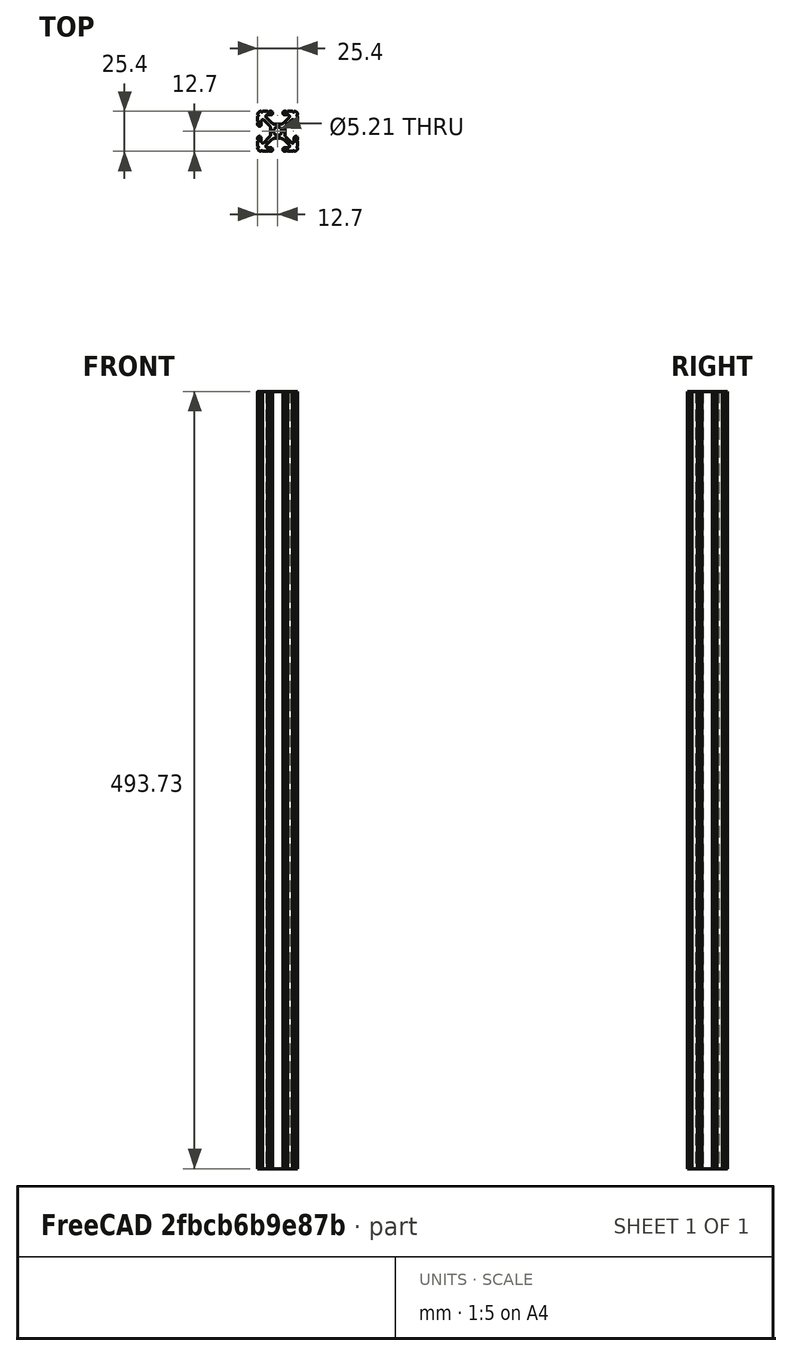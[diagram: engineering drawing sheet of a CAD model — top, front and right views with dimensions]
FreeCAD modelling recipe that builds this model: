
FCSTD DOCUMENT  (FreeCAD 0.18R4 (GitTag))
Label: 1010-19p438
License: All rights reserved
LicenseURL: http://en.wikipedia.org/wiki/All_rights_reserved
objects: Sketcher::SketchObject×1, Part::Extrusion×1
note: 2 computed .brp shape members not serialized (recipe doc carries the construction recipe); baked Part::Feature solids carry a one-line shape summary decoded from their .brp

FEATURE [Sketcher::SketchObject] Sketch097
  sketch-geometry (97):
    g0: Circle CenterX=0 CenterY=0 CenterZ=0 NormalX=0 NormalY=0 NormalZ=-1 AngleXU=0 Radius=2.6035
    g1: ArcOfCircle CenterX=12.7 CenterY=5.82508 CenterZ=0 NormalX=0 NormalY=0 NormalZ=1 AngleXU=0 Radius=0.508 StartAngle=1.5708 EndAngle=4.71239
    g2: LineSegment StartX=3.2385 StartY=11.651 StartZ=0 EndX=3.2385 EndY=11.5392 EndZ=0
    g3: LineSegment StartX=6.33313 StartY=-12.7 StartZ=0 EndX=9.55044 EndY=-12.7 EndZ=0
    g4: LineSegment StartX=7.20704 StartY=8.72437 StartZ=0 EndX=3.89827 EndY=5.42317 EndZ=0
    g5: ArcOfCircle CenterX=7.6835 CenterY=1.59319 CenterZ=0 NormalX=0 NormalY=0 NormalZ=1 AngleXU=0 Radius=3.175 StartAngle=2.35505 EndAngle=3.14159
    g6: ArcOfCircle CenterX=-1.70925 CenterY=-7.6708 CenterZ=0 NormalX=0 NormalY=0 NormalZ=1 AngleXU=0 Radius=3.175 StartAngle=1.5708 EndAngle=2.35528
    g7: ArcOfCircle CenterX=11.5392 CenterY=-4.28747 CenterZ=0 NormalX=0 NormalY=0 NormalZ=1 AngleXU=0 Radius=1.04901 StartAngle=1.5708 EndAngle=3.14159
    g8: ArcOfCircle CenterX=12.7 CenterY=-5.82508 CenterZ=0 NormalX=0 NormalY=0 NormalZ=1 AngleXU=0 Radius=0.508 StartAngle=1.5708 EndAngle=4.71239
    g9: LineSegment StartX=4.28751 StartY=10.4902 StartZ=0 EndX=6.47679 EndY=10.4902 EndZ=0
    g10: ArcOfCircle CenterX=4.28751 CenterY=11.651 CenterZ=0 NormalX=0 NormalY=0 NormalZ=1 AngleXU=0 Radius=1.04901 StartAngle=1.5708 EndAngle=3.14159
    g11: ArcOfCircle CenterX=6.47679 CenterY=9.45629 CenterZ=0 NormalX=0 NormalY=0 NormalZ=1 AngleXU=0 Radius=1.03391 StartAngle=5.49664 EndAngle=7.85398
    g12: ArcOfCircle CenterX=4.28751 CenterY=11.5392 CenterZ=0 NormalX=0 NormalY=0 NormalZ=1 AngleXU=0 Radius=1.04901 StartAngle=3.14159 EndAngle=4.71239
    g13: LineSegment StartX=3.95227 StartY=-5.42369 StartZ=0 EndX=7.17965 EndY=-8.64519 EndZ=0
    g14: ArcOfCircle CenterX=11.651 CenterY=4.28747 CenterZ=0 NormalX=0 NormalY=0 NormalZ=1 AngleXU=0 Radius=1.04901 StartAngle=4.71239 EndAngle=6.28319
    g15: ArcOfCircle CenterX=-5.82513 CenterY=-12.7 CenterZ=0 NormalX=0 NormalY=0 NormalZ=1 AngleXU=0 Radius=0.508 StartAngle=0 EndAngle=3.14159
    g16: LineSegment StartX=-6.47679 StartY=10.4902 StartZ=0 EndX=-4.28751 EndY=10.4902 EndZ=0
    g17: ArcOfCircle CenterX=-12.7 CenterY=10.0584 CenterZ=0 NormalX=0 NormalY=0 NormalZ=1 AngleXU=0 Radius=0.508 StartAngle=4.71239 EndAngle=7.85368
    g18: ArcOfCircle CenterX=-12.7 CenterY=5.82508 CenterZ=0 NormalX=0 NormalY=0 NormalZ=1 AngleXU=0 Radius=0.508 StartAngle=4.71239 EndAngle=7.85398
    g19: LineSegment StartX=-11.5392 StartY=-3.23846 StartZ=0 EndX=-11.651 EndY=-3.23846 EndZ=0
    g20: LineSegment StartX=-3.89827 StartY=5.42317 StartZ=0 EndX=-7.20704 EndY=8.72437 EndZ=0
    g21: LineSegment StartX=1.65578 StartY=4.4958 StartZ=0 EndX=-1.65578 EndY=4.4958 EndZ=0
    g22: ArcOfCircle CenterX=-1.65578 CenterY=7.6708 CenterZ=0 NormalX=0 NormalY=0 NormalZ=1 AngleXU=0 Radius=3.175 StartAngle=3.92813 EndAngle=4.71239
    g23: LineSegment StartX=-9.55044 StartY=-12.7 StartZ=0 EndX=-6.33313 EndY=-12.7 EndZ=0
    g24: ArcOfCircle CenterX=-5.82513 CenterY=12.7 CenterZ=0 NormalX=0 NormalY=0 NormalZ=1 AngleXU=0 Radius=0.508 StartAngle=3.14159 EndAngle=6.28319
    g25: ArcOfCircle CenterX=-4.28751 CenterY=11.651 CenterZ=0 NormalX=0 NormalY=0 NormalZ=1 AngleXU=0 Radius=1.04901 StartAngle=0 EndAngle=1.5708
    g26: LineSegment StartX=-12.7 StartY=-4.28747 StartZ=0 EndX=-12.7 EndY=-5.31708 EndZ=0
    g27: ArcOfCircle CenterX=-6.47679 CenterY=9.45629 CenterZ=0 NormalX=0 NormalY=0 NormalZ=1 AngleXU=0 Radius=1.03391 StartAngle=1.5708 EndAngle=3.92813
    g28: ArcOfCircle CenterX=-4.28751 CenterY=11.5392 CenterZ=0 NormalX=0 NormalY=0 NormalZ=1 AngleXU=0 Radius=1.04901 StartAngle=4.71239 EndAngle=6.28319
    g29: LineSegment StartX=-5.44101 StartY=-3.84082 StartZ=0 EndX=-8.73713 EndY=-7.12941 EndZ=0
    g30: ArcOfCircle CenterX=-7.6835 CenterY=-1.59319 CenterZ=0 NormalX=0 NormalY=0 NormalZ=1 AngleXU=0 Radius=3.175 StartAngle=5.49664 EndAngle=6.28319
    g31: LineSegment StartX=-12.7 StartY=5.31708 StartZ=0 EndX=-12.7 EndY=4.28747 EndZ=0
    g32: LineSegment StartX=-8.73713 StartY=7.12941 StartZ=0 EndX=-5.44101 EndY=3.84082 EndZ=0
    g33: LineSegment StartX=-11.651 StartY=3.23846 StartZ=0 EndX=-11.5392 EndY=3.23846 EndZ=0
    g34: ArcOfCircle CenterX=-9.46279 CenterY=-6.40209 CenterZ=0 NormalX=0 NormalY=0 NormalZ=1 AngleXU=0 Radius=1.02741 StartAngle=3.14159 EndAngle=5.49664
    g35: ArcOfCircle CenterX=-10.5918 CenterY=10.5918 CenterZ=0 NormalX=0 NormalY=0 NormalZ=1 AngleXU=0 Radius=2.1082 StartAngle=1.55877 EndAngle=3.15364
    g36: LineSegment StartX=-12.7 StartY=9.5504 StartZ=0 EndX=-12.7 EndY=6.33308 EndZ=0
    g37: LineSegment StartX=-6.33313 StartY=12.7 StartZ=0 EndX=-9.55044 EndY=12.7 EndZ=0
    g38: ArcOfCircle CenterX=-11.5392 CenterY=-4.28747 CenterZ=0 NormalX=0 NormalY=0 NormalZ=1 AngleXU=0 Radius=1.04901 StartAngle=0 EndAngle=1.5708
    g39: LineSegment StartX=4.28751 StartY=-12.7 StartZ=0 EndX=5.31713 EndY=-12.7 EndZ=0
    g40: LineSegment StartX=5.44101 StartY=3.84082 StartZ=0 EndX=8.73713 EndY=7.12941 EndZ=0
    g41: LineSegment StartX=10.4902 StartY=-4.28747 StartZ=0 EndX=10.4902 EndY=-6.40209 EndZ=0
    g42: ArcOfCircle CenterX=9.46279 CenterY=6.40209 CenterZ=0 NormalX=0 NormalY=0 NormalZ=1 AngleXU=0 Radius=1.02741 StartAngle=0 EndAngle=2.35505
    g43: ArcOfCircle CenterX=5.82513 CenterY=-12.7 CenterZ=0 NormalX=0 NormalY=0 NormalZ=1 AngleXU=0 Radius=0.508 StartAngle=0 EndAngle=3.14159
    g44: LineSegment StartX=12.7 StartY=-9.5504 StartZ=0 EndX=12.7 EndY=-6.33308 EndZ=0
    g45: LineSegment StartX=4.5085 StartY=-1.59319 StartZ=0 EndX=4.5085 EndY=1.59319 EndZ=0
    g46: ArcOfCircle CenterX=12.7 CenterY=10.0584 CenterZ=0 NormalX=0 NormalY=0 NormalZ=1 AngleXU=0 Radius=0.508 StartAngle=1.5711 EndAngle=4.71239
    g47: ArcOfCircle CenterX=12.7 CenterY=-10.0584 CenterZ=0 NormalX=0 NormalY=0 NormalZ=1 AngleXU=0 Radius=0.508 StartAngle=1.5708 EndAngle=4.71209
    g48: LineSegment StartX=3.2385 StartY=-11.5392 StartZ=0 EndX=3.2385 EndY=-11.651 EndZ=0
    g49: LineSegment StartX=8.73713 StartY=-7.12941 StartZ=0 EndX=5.44101 EndY=-3.84082 EndZ=0
    g50: ArcOfCircle CenterX=11.651 CenterY=-4.28747 CenterZ=0 NormalX=0 NormalY=0 NormalZ=1 AngleXU=0 Radius=1.04901 StartAngle=0 EndAngle=1.5708
    g51: ArcOfCircle CenterX=1.65578 CenterY=7.6708 CenterZ=0 NormalX=0 NormalY=0 NormalZ=1 AngleXU=0 Radius=3.175 StartAngle=4.71239 EndAngle=5.49664
    g52: ArcOfCircle CenterX=7.6835 CenterY=-1.59319 CenterZ=0 NormalX=0 NormalY=0 NormalZ=1 AngleXU=0 Radius=3.175 StartAngle=3.14159 EndAngle=3.92813
    g53: LineSegment StartX=12.7 StartY=4.28747 StartZ=0 EndX=12.7 EndY=5.31708 EndZ=0
    g54: ArcOfCircle CenterX=6.41641 CenterY=-9.40983 CenterZ=0 NormalX=0 NormalY=0 NormalZ=1 AngleXU=0 Radius=1.08037 StartAngle=4.71239 EndAngle=7.06949
    g55: LineSegment StartX=12.7 StartY=-5.31708 StartZ=0 EndX=12.7 EndY=-4.28747 EndZ=0
    g56: ArcOfCircle CenterX=10.0584 CenterY=-12.7 CenterZ=0 NormalX=0 NormalY=0 NormalZ=1 AngleXU=0 Radius=0.508 StartAngle=0.000300194 EndAngle=3.14159
    g57: ArcOfCircle CenterX=11.5392 CenterY=4.28747 CenterZ=0 NormalX=0 NormalY=0 NormalZ=1 AngleXU=0 Radius=1.04901 StartAngle=3.14159 EndAngle=4.71239
    g58: LineSegment StartX=12.7 StartY=6.33308 StartZ=0 EndX=12.7 EndY=9.5504 EndZ=0
    g59: ArcOfCircle CenterX=4.28751 CenterY=-11.5392 CenterZ=0 NormalX=0 NormalY=0 NormalZ=1 AngleXU=0 Radius=1.04901 StartAngle=1.5708 EndAngle=3.14159
    g60: ArcOfCircle CenterX=10.5918 CenterY=10.5918 CenterZ=0 NormalX=0 NormalY=0 NormalZ=1 AngleXU=0 Radius=2.1082 StartAngle=6.27114 EndAngle=7.86601
    g61: ArcOfCircle CenterX=9.46279 CenterY=-6.40209 CenterZ=0 NormalX=0 NormalY=0 NormalZ=1 AngleXU=0 Radius=1.02741 StartAngle=3.92813 EndAngle=6.28319
    g62: LineSegment StartX=6.41641 StartY=-10.4902 StartZ=0 EndX=4.28751 EndY=-10.4902 EndZ=0
    g63: LineSegment StartX=-10.4902 StartY=-6.40209 StartZ=0 EndX=-10.4902 EndY=-4.28747 EndZ=0
    g64: ArcOfCircle CenterX=-9.46279 CenterY=6.40209 CenterZ=0 NormalX=0 NormalY=0 NormalZ=1 AngleXU=0 Radius=1.02741 StartAngle=0.786542 EndAngle=3.14159
    g65: LineSegment StartX=-10.4902 StartY=4.28747 StartZ=0 EndX=-10.4902 EndY=6.40209 EndZ=0
    g66: LineSegment StartX=-4.5085 StartY=1.59319 StartZ=0 EndX=-4.5085 EndY=-1.59319 EndZ=0
    g67: LineSegment StartX=-4.28751 StartY=12.7 StartZ=0 EndX=-5.31713 EndY=12.7 EndZ=0
    g68: ArcOfCircle CenterX=-11.5392 CenterY=4.28747 CenterZ=0 NormalX=0 NormalY=0 NormalZ=1 AngleXU=0 Radius=1.04901 StartAngle=4.71239 EndAngle=6.28319
    g69: LineSegment StartX=-3.2385 StartY=11.5392 StartZ=0 EndX=-3.2385 EndY=11.651 EndZ=0
    g70: ArcOfCircle CenterX=-11.651 CenterY=4.28747 CenterZ=0 NormalX=0 NormalY=0 NormalZ=1 AngleXU=0 Radius=1.04901 StartAngle=3.14159 EndAngle=4.71239
    g71: ArcOfCircle CenterX=-7.6835 CenterY=1.59319 CenterZ=0 NormalX=0 NormalY=0 NormalZ=1 AngleXU=0 Radius=3.175 StartAngle=0 EndAngle=0.786542
    g72: ArcOfCircle CenterX=-10.0584 CenterY=12.7 CenterZ=0 NormalX=0 NormalY=0 NormalZ=1 AngleXU=0 Radius=0.508 StartAngle=3.14189 EndAngle=6.28319
    g73: LineSegment StartX=-1.70925 StartY=-4.4958 StartZ=0 EndX=1.70925 EndY=-4.4958 EndZ=0
    g74: LineSegment StartX=11.651 StartY=-3.23846 StartZ=0 EndX=11.5392 EndY=-3.23846 EndZ=0
    g75: ArcOfCircle CenterX=-10.5918 CenterY=-10.5918 CenterZ=0 NormalX=0 NormalY=0 NormalZ=1 AngleXU=0 Radius=2.1082 StartAngle=3.12954 EndAngle=4.72442
    g76: ArcOfCircle CenterX=10.5918 CenterY=-10.5918 CenterZ=0 NormalX=0 NormalY=0 NormalZ=1 AngleXU=0 Radius=2.1082 StartAngle=4.70036 EndAngle=6.29523
    g77: ArcOfCircle CenterX=-12.7 CenterY=-5.82508 CenterZ=0 NormalX=0 NormalY=0 NormalZ=1 AngleXU=0 Radius=0.508 StartAngle=4.71239 EndAngle=7.85398
    g78: ArcOfCircle CenterX=5.82513 CenterY=12.7 CenterZ=0 NormalX=0 NormalY=0 NormalZ=1 AngleXU=0 Radius=0.508 StartAngle=3.14159 EndAngle=6.28319
    g79: LineSegment StartX=9.55044 StartY=12.7 StartZ=0 EndX=6.33313 EndY=12.7 EndZ=0
    g80: ArcOfCircle CenterX=10.0584 CenterY=12.7 CenterZ=0 NormalX=0 NormalY=0 NormalZ=1 AngleXU=0 Radius=0.508 StartAngle=3.14159 EndAngle=6.28289
    g81: ArcOfCircle CenterX=1.70925 CenterY=-7.6708 CenterZ=0 NormalX=0 NormalY=0 NormalZ=1 AngleXU=0 Radius=3.175 StartAngle=0.78631 EndAngle=1.5708
    g82: ArcOfCircle CenterX=4.28751 CenterY=-11.651 CenterZ=0 NormalX=0 NormalY=0 NormalZ=1 AngleXU=0 Radius=1.04901 StartAngle=3.14159 EndAngle=4.71239
    g83: LineSegment StartX=5.31713 StartY=12.7 StartZ=0 EndX=4.28751 EndY=12.7 EndZ=0
    g84: LineSegment StartX=10.4902 StartY=6.40209 StartZ=0 EndX=10.4902 EndY=4.28747 EndZ=0
    g85: LineSegment StartX=11.5392 StartY=3.23846 StartZ=0 EndX=11.651 EndY=3.23846 EndZ=0
    g86: ArcOfCircle CenterX=-10.0584 CenterY=-12.7 CenterZ=0 NormalX=0 NormalY=0 NormalZ=1 AngleXU=0 Radius=0.508 StartAngle=0 EndAngle=3.14129
    g87: ArcOfCircle CenterX=-12.7 CenterY=-10.0584 CenterZ=0 NormalX=0 NormalY=0 NormalZ=1 AngleXU=0 Radius=0.508 StartAngle=4.71269 EndAngle=7.85398
    g88: ArcOfCircle CenterX=-4.28751 CenterY=-11.5392 CenterZ=0 NormalX=0 NormalY=0 NormalZ=1 AngleXU=0 Radius=1.04901 StartAngle=0 EndAngle=1.5708
    g89: ArcOfCircle CenterX=-4.28751 CenterY=-11.651 CenterZ=0 NormalX=0 NormalY=0 NormalZ=1 AngleXU=0 Radius=1.04901 StartAngle=4.71239 EndAngle=6.28319
    g90: LineSegment StartX=-12.7 StartY=-6.33308 StartZ=0 EndX=-12.7 EndY=-9.5504 EndZ=0
    g91: ArcOfCircle CenterX=-11.651 CenterY=-4.28747 CenterZ=0 NormalX=0 NormalY=0 NormalZ=1 AngleXU=0 Radius=1.04901 StartAngle=1.5708 EndAngle=3.14159
    g92: LineSegment StartX=-7.17965 StartY=-8.64519 StartZ=0 EndX=-3.95227 EndY=-5.42369 EndZ=0
    g93: LineSegment StartX=-5.31713 StartY=-12.7 StartZ=0 EndX=-4.28751 EndY=-12.7 EndZ=0
    g94: LineSegment StartX=-3.2385 StartY=-11.651 StartZ=0 EndX=-3.2385 EndY=-11.5392 EndZ=0
    g95: ArcOfCircle CenterX=-6.41641 CenterY=-9.40983 CenterZ=0 NormalX=0 NormalY=0 NormalZ=1 AngleXU=0 Radius=1.08037 StartAngle=2.35528 EndAngle=4.71239
    g96: LineSegment StartX=-4.28751 StartY=-10.4902 StartZ=0 EndX=-6.41641 EndY=-10.4902 EndZ=0
FEATURE [Part::Extrusion] Extrude
  Base = -> Sketch097
  Dir = (0,0,1)
  DirMode = 2
  FaceMakerClass = Part::FaceMakerBullseye
  LengthFwd = 493.725
  LengthRev = 0
  Solid = true
  Symmetric = false
